# Revit family: Calming Corner_Wellness and Mindfulness
name_source: partatom
category: Furniture Systems
units: mm (PartAtom-declared; Revit-internal decimal feet)

## family parameters
Always vertical = Yes
Cut with Voids When Loaded = No
Part Type = Normal
Room Calculation Point = No
Round Connector Dimension = Use Diameter
Shared = No
Work Plane-Based = No

## types (1)
- Calming Corner_Wellness and Mindfulness
    3" Leaf Lily pad Seat fabric - 1 = <By Category>
    3" Leaf Lily pad Seat fabric - 2 = <By Category>
    3" Leaf Lily pad Side fabric - 1 = <By Category>
    3" Leaf Lily pad Side fabric - 2 = <By Category>
    6" Leaf Lily pad Seat fabric = <By Category>
    6" Leaf Lily pad Side fabric = <By Category>
    Manufacturer = FOMCORE
    Model = Calming Corner_Wellness and Mindfulness
    Rock'n Roller Back Fabric = <By Category>
    Rock'n Roller Seat Fabric = <By Category>
    Type Comments = COMBO UNIT
    URL = https://fomcore.com

## geometry (parser evidence)
native form markers: Sweep x16
no freeform markers — native parametric forms only
